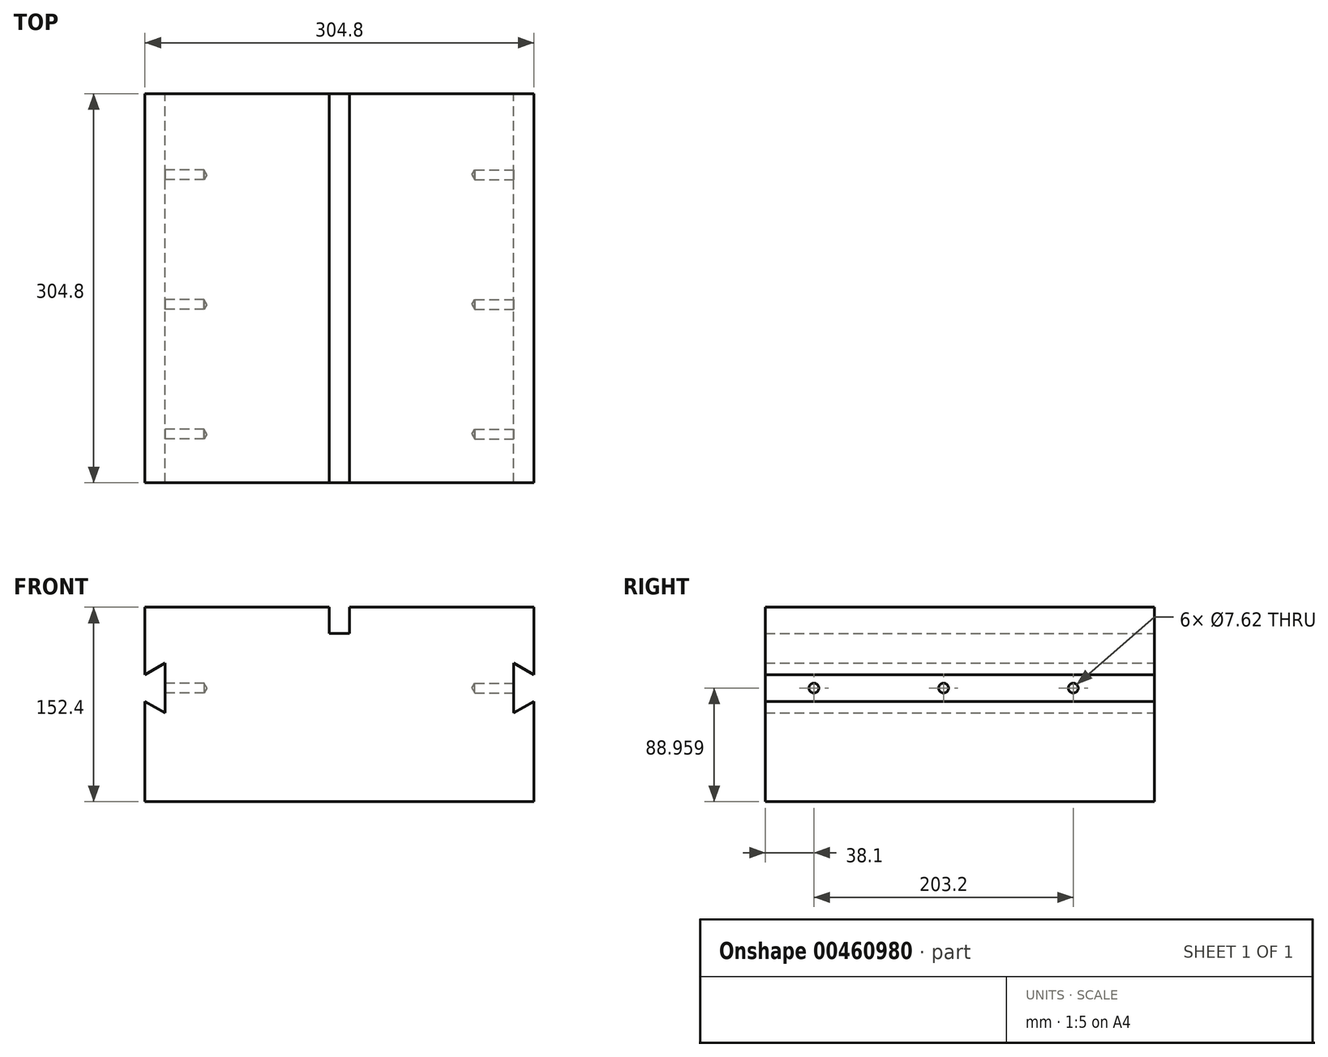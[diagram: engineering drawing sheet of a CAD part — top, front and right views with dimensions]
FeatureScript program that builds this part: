
annotation { "Feature Type Name" : "Feature", "Feature Type Description" : "" }
export const myFeature = defineFeature(function(context is Context, id is Id, definition is map)
    precondition{}
    {
        {
            var Q0;
            Q0=qCreatedBy(makeId("Front.planeOp"),FACE);
            var sketch = newSketch(context, id + "F0", { "sketchPlane" : qUnion([Q0])});
            skLineSegment(sketch, "E0.bottom", {"start": v(-183.49, 51.04) * mm, "end": v(-39.02, 51.04) * mm});
            skLineSegment(sketch, "E0.top", {"start": v(-183.49, -101.36) * mm, "end": v(121.31, -101.36) * mm});
            skLineSegment(sketch, "E0.left", {"start": v(-183.49, 51.04) * mm, "end": v(-183.49, -2.05) * mm});
            skLineSegment(sketch, "E0.right", {"start": v(121.31, 51.04) * mm, "end": v(121.31, -2.05) * mm});
            skLineSegment(sketch, "E1.0", {"start": v(-23.15, 51.04) * mm, "end": v(-23.15, 30.46) * mm});
            skLineSegment(sketch, "E2.0", {"start": v(-39.02, 51.04) * mm, "end": v(-39.02, 30.46) * mm});
            skLineSegment(sketch, "E3", {"start": v(-39.02, 30.46) * mm, "end": v(-23.15, 30.46) * mm});
            skLineSegment(sketch, "E4.trimOffspring", {"start": v(-23.15, 51.04) * mm, "end": v(121.31, 51.04) * mm});
            skLineSegment(sketch, "E5", {"start": v(121.31, -22.75) * mm, "end": v(105.44, -31.92) * mm});
            skLineSegment(sketch, "E6", {"start": v(121.31, -2.05) * mm, "end": v(105.44, 7.11) * mm});
            skLineSegment(sketch, "E7", {"start": v(105.44, 7.11) * mm, "end": v(105.44, -31.92) * mm});
            skLineSegment(sketch, "E8.trimOffspring", {"start": v(121.31, -22.75) * mm, "end": v(121.31, -101.36) * mm});
            skPoint(sketch, "E9.end.orphan", {"position": v(77.17, -2.05) * mm});
            skPoint(sketch, "E10.end.orphan", {"position": v(77.17, -22.75) * mm});
            skLineSegment(sketch, "E11", {"start": v(-31.09, -101.36) * mm, "end": v(-31.09, 30.46) * mm});
            skLineSegment(sketch, "E12.MirrorCS", {"start": v(-183.49, -2.05) * mm, "end": v(-167.61, 7.11) * mm});
            skLineSegment(sketch, "E13.MirrorCS", {"start": v(-167.61, 7.11) * mm, "end": v(-167.61, -31.92) * mm});
            skLineSegment(sketch, "E14.MirrorCS", {"start": v(-183.49, -22.75) * mm, "end": v(-167.61, -31.92) * mm});
            skLineSegment(sketch, "E15.trimOffspring", {"start": v(-183.49, -22.75) * mm, "end": v(-183.49, -101.36) * mm});
            skSolve(sketch);
        }
        {
            var Q0;
            Q0 = qSketchRegion(id + "F0", true);
            extrude(context, id + "F1", {"entities" : qUnion([Q0]), "depth" : 304.8 * mm, "offsetDistance" : 25.4 * mm});
        }
        {
            var Q0;
            Q0=makeQuery(id+"F1.opExtrude","SWEPT_FACE",FACE,{"disambiguationData":[OSD([sQuery(id+"F0.wireOp",EDGE,"E7")])]});
            var sketch = newSketch(context, id + "F2", { "sketchPlane" : qUnion([Q0])});
            skPoint(sketch, "E16", {"position": v(0, -12.4) * mm});
            skPoint(sketch, "E17", {"position": v(-63.5, -12.4) * mm});
            skPoint(sketch, "E18", {"position": v(-165.1, -12.4) * mm});
            skPoint(sketch, "E19", {"position": v(-266.7, -12.4) * mm});
            skSolve(sketch);
        }
        {
            var Q0;
            Q0=makeQuery(id+"F1.opExtrude","SWEPT_FACE",FACE,{"disambiguationData":[OSD([sQuery(id+"F0.wireOp",EDGE,"E13.MirrorCS")])]});
            var sketch = newSketch(context, id + "F3", { "sketchPlane" : qUnion([Q0])});
            skPoint(sketch, "E20", {"position": v(63.5, -12.4) * mm});
            skPoint(sketch, "E20.positionSnap0", {"position": v(0, -12.4) * mm});
            skPoint(sketch, "E21", {"position": v(165.1, -12.4) * mm});
            skPoint(sketch, "E22", {"position": v(266.7, -12.4) * mm});
            skSolve(sketch);
        }
        {
            var Q0;
            Q0=sQuery(id+"F2.wireOp",VERTEX,"E17");
            var Q1;
            Q1=sQuery(id+"F2.wireOp",VERTEX,"E18");
            var Q2;
            Q2=sQuery(id+"F2.wireOp",VERTEX,"E19");
            var Q3;
            Q3=makeQuery(id+"F1.opExtrude","SWEPT_BODY",BODY,{"disambiguationData":[OSD([sQuery(id+"F0.wireOp",EDGE,"E0.bottom"),sQuery(id+"F0.wireOp",EDGE,"E0.top"),sQuery(id+"F0.wireOp",EDGE,"E0.left"),sQuery(id+"F0.wireOp",EDGE,"E0.right"),sQuery(id+"F0.wireOp",EDGE,"E1.0"),sQuery(id+"F0.wireOp",EDGE,"E2.0"),sQuery(id+"F0.wireOp",EDGE,"E3"),sQuery(id+"F0.wireOp",EDGE,"E4.trimOffspring"),sQuery(id+"F0.wireOp",EDGE,"E5"),sQuery(id+"F0.wireOp",EDGE,"E6"),sQuery(id+"F0.wireOp",EDGE,"E7"),sQuery(id+"F0.wireOp",EDGE,"E8.trimOffspring"),sQuery(id+"F0.wireOp",EDGE,"E12.MirrorCS"),sQuery(id+"F0.wireOp",EDGE,"E13.MirrorCS"),sQuery(id+"F0.wireOp",EDGE,"E14.MirrorCS"),sQuery(id+"F0.wireOp",EDGE,"E15.trimOffspring")])]});
            hole(context, id + "F4", {"style" : HoleStyle.SIMPLE, "endStyle" : HoleEndStyle.BLIND, "holeDiameter" : 7.62 * mm, "holeDepth" : 30.48 * mm, "isTappedThrough" : true, "tappedDepth" : 12.7 * mm, "tapClearance" : 3, "startFromSketch" : true, "locations" : qUnion([Q0, Q1, Q2]), "scope" : qUnion([Q3])});
        }
        {
            var Q0;
            Q0=sQuery(id+"F3.wireOp",VERTEX,"E20");
            var Q1;
            Q1=sQuery(id+"F3.wireOp",VERTEX,"E21");
            var Q2;
            Q2=sQuery(id+"F3.wireOp",VERTEX,"E22");
            var Q3;
            Q3=makeQuery(id+"F1.opExtrude","SWEPT_BODY",BODY,{"disambiguationData":[OSD([sQuery(id+"F0.wireOp",EDGE,"E0.bottom"),sQuery(id+"F0.wireOp",EDGE,"E0.top"),sQuery(id+"F0.wireOp",EDGE,"E0.left"),sQuery(id+"F0.wireOp",EDGE,"E0.right"),sQuery(id+"F0.wireOp",EDGE,"E1.0"),sQuery(id+"F0.wireOp",EDGE,"E2.0"),sQuery(id+"F0.wireOp",EDGE,"E3"),sQuery(id+"F0.wireOp",EDGE,"E4.trimOffspring"),sQuery(id+"F0.wireOp",EDGE,"E5"),sQuery(id+"F0.wireOp",EDGE,"E6"),sQuery(id+"F0.wireOp",EDGE,"E7"),sQuery(id+"F0.wireOp",EDGE,"E8.trimOffspring"),sQuery(id+"F0.wireOp",EDGE,"E12.MirrorCS"),sQuery(id+"F0.wireOp",EDGE,"E13.MirrorCS"),sQuery(id+"F0.wireOp",EDGE,"E14.MirrorCS"),sQuery(id+"F0.wireOp",EDGE,"E15.trimOffspring")])]});
            hole(context, id + "F5", {"style" : HoleStyle.SIMPLE, "endStyle" : HoleEndStyle.BLIND, "holeDiameter" : 7.62 * mm, "holeDepth" : 30.48 * mm, "isTappedThrough" : true, "tappedDepth" : 12.7 * mm, "tapClearance" : 3, "startFromSketch" : true, "locations" : qUnion([Q0, Q1, Q2]), "scope" : qUnion([Q3])});
        }
    });
